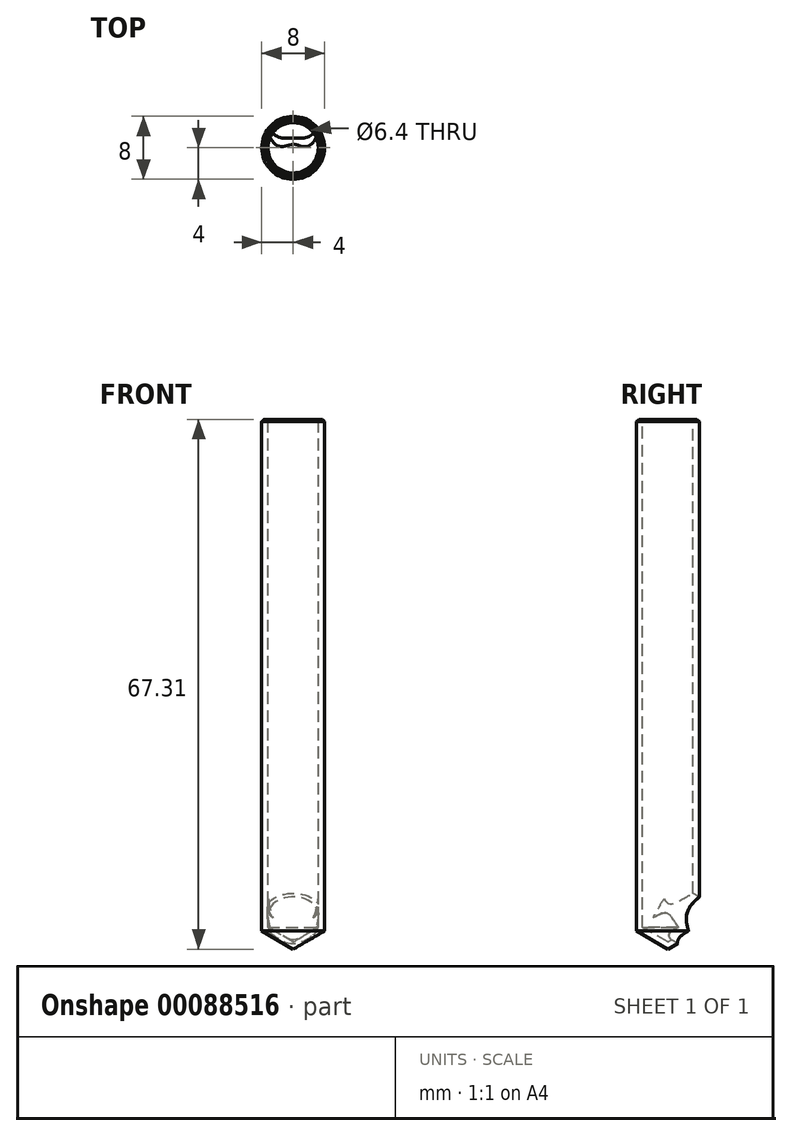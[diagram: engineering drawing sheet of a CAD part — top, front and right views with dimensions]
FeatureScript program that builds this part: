
annotation { "Feature Type Name" : "Feature", "Feature Type Description" : "" }
export const myFeature = defineFeature(function(context is Context, id is Id, definition is map)
    precondition{}
    {
        {
            var Q0;
            Q0=qCreatedBy(makeId("Front.planeOp"),FACE);
            var sketch = newSketch(context, id + "F0", { "sketchPlane" : qUnion([Q0])});
            skLineSegment(sketch, "E0", {"start": v(0, 0) * mm, "end": v(-66.29, 0) * mm});
            skSolve(sketch);
        }
        {
            var Q0;
            Q0=sQuery(id+"F0.wireOp",EDGE,"E0");
            cPlane(context, id + "F1", {"entities" : qUnion([Q0]), "cplaneType" : CPlaneType.LINE_ANGLE, "offset" : 150 * mm, "angle" : 30 * degree, "width" : 150 * mm, "height" : 150 * mm});
        }
        {
            var Q0;
            Q0=qCreatedBy(makeId("Front.planeOp"),FACE);
            var sketch = newSketch(context, id + "F2", { "sketchPlane" : qUnion([Q0])});
            skLineSegment(sketch, "E1", {"start": v(0, 0) * mm, "end": v(0, -65.43) * mm, "construction": true});
            skLineSegment(sketch, "E2", {"start": v(3.2, 0) * mm, "end": v(3.2, -64.54) * mm});
            skLineSegment(sketch, "E3", {"start": v(0, -67.3) * mm, "end": v(4, -65) * mm});
            skLineSegment(sketch, "E4", {"start": v(4, -65) * mm, "end": v(4, 0) * mm});
            skLineSegment(sketch, "E5", {"start": v(4, 0) * mm, "end": v(3.2, 0) * mm});
            skLineSegment(sketch, "E6", {"start": v(3.2, -64.54) * mm, "end": v(0, -66.39) * mm});
            skLineSegment(sketch, "E7", {"start": v(0, -67.3) * mm, "end": v(0, -66.39) * mm});
            skSolve(sketch);
        }
        {
            var Q0;
            Q0 = qSketchRegion(id + "F2", true);
            var Q1;
            Q1=sQuery(id+"F2.wireOp",EDGE,"E1");
            revolve(context, id + "F3", {"entities" : qUnion([Q0]), "axis" : qUnion([Q1]), "revolveType" : RevolveType.FULL});
        }
        {
            var Q0;
            Q0=makeQuery(id+"F3.opRevolve","SWEPT_EDGE",EDGE,{"disambiguationData":[OSD([sQuery(id+"F2.wireOp",EDGE,"E4"),sQuery(id+"F2.wireOp",EDGE,"E5")])]});
            var Q1;
            Q1=makeQuery(id+"F3.opRevolve","SWEPT_EDGE",EDGE,{"disambiguationData":[OSD([sQuery(id+"F2.wireOp",EDGE,"E2"),sQuery(id+"F2.wireOp",EDGE,"E5")])]});
            chamfer(context, id + "F4", {"entities" : qUnion([Q0, Q1]), "width" : .3 * mm, "tangentPropagation" : true});
        }
        {
            var Q0;
            Q0=qCreatedBy(id+"F1.planeOp",FACE);
            var sketch = newSketch(context, id + "F5", { "sketchPlane" : qUnion([Q0])});
            skCircle(sketch, "E8", {"center": v(0, -53.8) * mm, "radius": 3.25 * mm});
            skSolve(sketch);
        }
        {
            var Q0;
            Q0=makeQuery(id+"F5.imprint","IMPRINT",FACE,{"disambiguationData":[TD([[makeQuery(id+"F5.imprint","IMPRINT",EDGE,{"derivedFrom":sQuery(id+"F5.wireOp",EDGE,"E8")}),1.0]])]});
            extrude(context, id + "F6", {"entities" : qUnion([Q0]), "operationType" : NewBodyOperationType.REMOVE, "endBound" : BoundingType.THROUGH_ALL, "oppositeDirection" : true, "depth" : 50 * mm, "hasSecondDirection" : true, "secondDirectionOppositeDirection" : true, "secondDirectionDepth" : 30 * mm});
        }
    });
